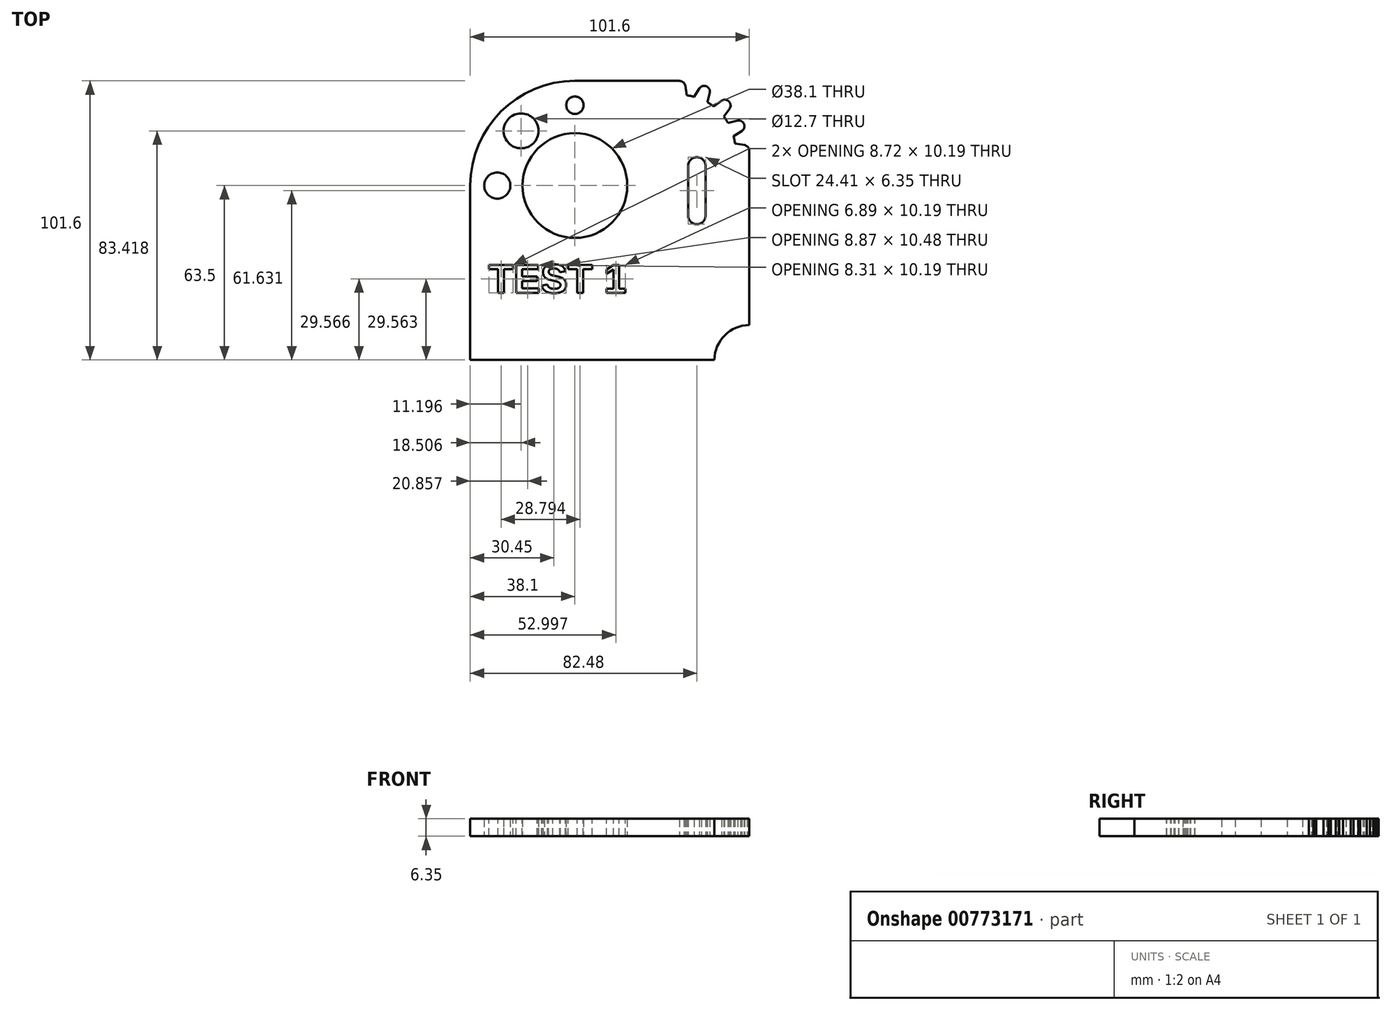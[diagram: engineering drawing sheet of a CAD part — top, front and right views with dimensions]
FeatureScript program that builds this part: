
annotation { "Feature Type Name" : "Feature", "Feature Type Description" : "" }
export const myFeature = defineFeature(function(context is Context, id is Id, definition is map)
    precondition{}
    {
        {
            var Q0;
            Q0=qCreatedBy(makeId("Top.planeOp"),FACE);
            var sketch = newSketch(context, id + "F0", { "sketchPlane" : qUnion([Q0])});
            skLineSegment(sketch, "E0.bottom", {"start": v(-12.7, 0) * mm, "end": v(-101.6, 0) * mm});
            skLineSegment(sketch, "E0.top", {"start": v(-25.4, 101.6) * mm, "end": v(-63.5, 101.6) * mm});
            skLineSegment(sketch, "E0.left", {"start": v(0, 12.7) * mm, "end": v(0, 76.2) * mm});
            skLineSegment(sketch, "E0.right", {"start": v(-101.6, 0) * mm, "end": v(-101.6, 63.5) * mm});
            skPoint(sketch, "E1.visualSharp", {"position": v(-101.6, 101.6) * mm});
            skArc(sketch, "E1.filletArc", {"start": v(-63.5, 101.6) * mm, "mid": v(-90.44, 90.44) * mm, "end": v(-101.6, 63.5) * mm});
            skArc(sketch, "E2.0", {"start": v(-5.08, 76.2) * mm, "mid": v(-11.03, 90.57) * mm, "end": v(-25.4, 96.52) * mm});
            skLineSegment(sketch, "E3", {"start": v(-25.4, 96.52) * mm, "end": v(-25.4, 101.6) * mm});
            skLineSegment(sketch, "E4", {"start": v(-5.08, 76.2) * mm, "end": v(0, 76.2) * mm});
            skLineSegment(sketch, "E5", {"start": v(-22.77, 96.35) * mm, "end": v(-23.3, 99.9) * mm});
            skLineSegment(sketch, "E6", {"start": v(-23.3, 99.9) * mm, "end": v(-23.77, 100.84) * mm});
            skArc(sketch, "E7", {"start": v(-23.77, 100.84) * mm, "mid": v(-24.52, 101.35) * mm, "end": v(-25.4, 101.6) * mm});
            skLineSegment(sketch, "E8.1.0", {"start": v(-15.26, 93.81) * mm, "end": v(-14.4, 97.29) * mm});
            skLineSegment(sketch, "E8.1.1", {"start": v(-14.4, 97.29) * mm, "end": v(-14.47, 98.34) * mm});
            skArc(sketch, "E8.1.2", {"start": v(-14.47, 98.34) * mm, "mid": v(-14.96, 99.1) * mm, "end": v(-15.68, 99.67) * mm});
            skArc(sketch, "E8.1.3", {"start": v(-17.48, 99.58) * mm, "mid": v(-16.59, 99.78) * mm, "end": v(-15.68, 99.67) * mm});
            skLineSegment(sketch, "E8.1.4", {"start": v(-18.27, 98.9) * mm, "end": v(-17.48, 99.58) * mm});
            skLineSegment(sketch, "E8.1.5", {"start": v(-20.12, 95.82) * mm, "end": v(-18.27, 98.9) * mm});
            skLineSegment(sketch, "E8.2.0", {"start": v(-9.3, 88.59) * mm, "end": v(-7.16, 91.47) * mm});
            skLineSegment(sketch, "E8.2.1", {"start": v(-7.16, 91.47) * mm, "end": v(-6.83, 92.47) * mm});
            skArc(sketch, "E8.2.2", {"start": v(-6.83, 92.47) * mm, "mid": v(-7, 93.36) * mm, "end": v(-7.44, 94.16) * mm});
            skArc(sketch, "E8.2.3", {"start": v(-9.13, 94.77) * mm, "mid": v(-8.24, 94.6) * mm, "end": v(-7.44, 94.16) * mm});
            skLineSegment(sketch, "E8.2.4", {"start": v(-10.13, 94.44) * mm, "end": v(-9.13, 94.77) * mm});
            skLineSegment(sketch, "E8.2.5", {"start": v(-13.01, 92.3) * mm, "end": v(-10.13, 94.44) * mm});
            skLineSegment(sketch, "E8.3.0", {"start": v(-5.78, 81.48) * mm, "end": v(-2.7, 83.33) * mm});
            skLineSegment(sketch, "E8.3.1", {"start": v(-2.7, 83.33) * mm, "end": v(-2.02, 84.12) * mm});
            skArc(sketch, "E8.3.2", {"start": v(-2.02, 84.12) * mm, "mid": v(-1.82, 85.01) * mm, "end": v(-1.93, 85.92) * mm});
            skArc(sketch, "E8.3.3", {"start": v(-3.26, 87.13) * mm, "mid": v(-2.5, 86.64) * mm, "end": v(-1.93, 85.92) * mm});
            skLineSegment(sketch, "E8.3.4", {"start": v(-4.31, 87.2) * mm, "end": v(-3.26, 87.13) * mm});
            skLineSegment(sketch, "E8.3.5", {"start": v(-7.79, 86.34) * mm, "end": v(-4.31, 87.2) * mm});
            skArc(sketch, "E8.4.3", {"start": v(-0.76, 77.83) * mm, "mid": v(-0.25, 77.08) * mm, "end": v(0, 76.2) * mm});
            skLineSegment(sketch, "E8.4.4", {"start": v(-1.7, 78.3) * mm, "end": v(-0.76, 77.83) * mm});
            skLineSegment(sketch, "E8.4.5", {"start": v(-5.25, 78.83) * mm, "end": v(-1.7, 78.3) * mm});
            skLineSegment(sketch, "E8.anchor1", {"start": v(-25.4, 76.2) * mm, "end": v(-25.4, 101.6) * mm, "construction": true});
            skLineSegment(sketch, "E8.anchor2", {"start": v(-25.4, 76.2) * mm, "end": v(0, 76.2) * mm, "construction": true});
            skArc(sketch, "E9", {"start": v(0, 12.7) * mm, "mid": v(-8.98, 8.98) * mm, "end": v(-12.7, 0) * mm});
            skCircle(sketch, "E10", {"center": v(-63.5, 63.5) * mm, "radius": 19.05 * mm});
            skCircle(sketch, "E11", {"center": v(-63.5, 92.75) * mm, "radius": 3.18 * mm});
            skCircle(sketch, "E12", {"center": v(-91.76, 63.5) * mm, "radius": 4.76 * mm});
            skCircle(sketch, "E13", {"center": v(-83.1, 83.42) * mm, "radius": 6.35 * mm});
            skArc(sketch, "E14", {"start": v(-15.95, 70.66) * mm, "mid": v(-19.12, 73.84) * mm, "end": v(-22.3, 70.66) * mm});
            skArc(sketch, "E15", {"start": v(-22.3, 52.6) * mm, "mid": v(-19.12, 49.42) * mm, "end": v(-15.95, 52.6) * mm});
            skLineSegment(sketch, "E16", {"start": v(-15.95, 52.6) * mm, "end": v(-15.95, 70.66) * mm});
            skLineSegment(sketch, "E17", {"start": v(-22.3, 52.6) * mm, "end": v(-22.3, 70.66) * mm});
            skSolve(sketch);
        }
        {
            var Q0;
            Q0=makeQuery(id+"F0.imprint","IMPRINT",FACE,{"disambiguationData":[TD([[makeQuery(id+"F0.imprint","IMPRINT",EDGE,{"derivedFrom":sQuery(id+"F0.wireOp",EDGE,"E0.bottom")}),-1.0]])]});
            var Q1;
            {var subQ1=sQuery(id+"F0.wireOp",EDGE,"E3");Q1=makeQuery(id+"F0.imprint","IMPRINT",FACE,{"disambiguationData":[TD([[makeQuery(id+"F0.imprint","IMPRINT",EDGE,{"derivedFrom":subQ1}),-1.0]])]});}
            var Q2;
            {var subQ0=sQuery(id+"F0.wireOp",EDGE,"E8.1.0");Q2=makeQuery(id+"F0.imprint","IMPRINT",FACE,{"disambiguationData":[TD([[makeQuery(id+"F0.imprint","IMPRINT",EDGE,{"derivedFrom":subQ0}),1.0]])]});}
            var Q3;
            {var subQ0=sQuery(id+"F0.wireOp",EDGE,"E8.2.0");Q3=makeQuery(id+"F0.imprint","IMPRINT",FACE,{"disambiguationData":[TD([[makeQuery(id+"F0.imprint","IMPRINT",EDGE,{"derivedFrom":subQ0}),1.0]])]});}
            var Q4;
            {var subQ0=sQuery(id+"F0.wireOp",EDGE,"E8.3.0");Q4=makeQuery(id+"F0.imprint","IMPRINT",FACE,{"disambiguationData":[TD([[makeQuery(id+"F0.imprint","IMPRINT",EDGE,{"derivedFrom":subQ0}),1.0]])]});}
            var Q5;
            {var subQ0=sQuery(id+"F0.wireOp",EDGE,"E4");Q5=makeQuery(id+"F0.imprint","IMPRINT",FACE,{"disambiguationData":[TD([[makeQuery(id+"F0.imprint","IMPRINT",EDGE,{"derivedFrom":subQ0}),1.0]])]});}
            extrude(context, id + "F1", {"entities" : qUnion([Q0, Q1, Q2, Q3, Q4, Q5]), "depth" : 6.35 * mm, "offsetDistance" : 25.4 * mm});
        }
        {
            var Q0;
            Q0=makeQuery(id+"F1.opExtrude","CAP_FACE",FACE,{"disambiguationData":[OSD([sQuery(id+"F0.wireOp",EDGE,"E0.bottom"),sQuery(id+"F0.wireOp",EDGE,"E0.top"),sQuery(id+"F0.wireOp",EDGE,"E0.left"),sQuery(id+"F0.wireOp",EDGE,"E0.right"),sQuery(id+"F0.wireOp",EDGE,"E1.filletArc"),sQuery(id+"F0.wireOp",EDGE,"E2.0"),sQuery(id+"F0.wireOp",EDGE,"E5"),sQuery(id+"F0.wireOp",EDGE,"E6"),sQuery(id+"F0.wireOp",EDGE,"E7"),sQuery(id+"F0.wireOp",EDGE,"E8.1.0"),sQuery(id+"F0.wireOp",EDGE,"E8.1.1"),sQuery(id+"F0.wireOp",EDGE,"E8.1.2"),sQuery(id+"F0.wireOp",EDGE,"E8.1.3"),sQuery(id+"F0.wireOp",EDGE,"E8.1.4"),sQuery(id+"F0.wireOp",EDGE,"E8.1.5"),sQuery(id+"F0.wireOp",EDGE,"E8.2.0"),sQuery(id+"F0.wireOp",EDGE,"E8.2.1"),sQuery(id+"F0.wireOp",EDGE,"E8.2.2"),sQuery(id+"F0.wireOp",EDGE,"E8.2.3"),sQuery(id+"F0.wireOp",EDGE,"E8.2.4"),sQuery(id+"F0.wireOp",EDGE,"E8.2.5"),sQuery(id+"F0.wireOp",EDGE,"E8.3.0"),sQuery(id+"F0.wireOp",EDGE,"E8.3.1"),sQuery(id+"F0.wireOp",EDGE,"E8.3.2"),sQuery(id+"F0.wireOp",EDGE,"E8.3.3"),sQuery(id+"F0.wireOp",EDGE,"E8.3.4"),sQuery(id+"F0.wireOp",EDGE,"E8.3.5"),sQuery(id+"F0.wireOp",EDGE,"E8.4.3"),sQuery(id+"F0.wireOp",EDGE,"E8.4.4"),sQuery(id+"F0.wireOp",EDGE,"E8.4.5"),sQuery(id+"F0.wireOp",EDGE,"E9"),sQuery(id+"F0.wireOp",EDGE,"E10"),sQuery(id+"F0.wireOp",EDGE,"E11"),sQuery(id+"F0.wireOp",EDGE,"E12"),sQuery(id+"F0.wireOp",EDGE,"E13"),sQuery(id+"F0.wireOp",EDGE,"E14"),sQuery(id+"F0.wireOp",EDGE,"E15"),sQuery(id+"F0.wireOp",EDGE,"E16"),sQuery(id+"F0.wireOp",EDGE,"E17")])],"isStart":false});
            var sketch = newSketch(context, id + "F2", { "sketchPlane" : qUnion([Q0])});
            skText(sketch, "E18", { "text": "TEST 1", "fontName": "Arimo-Bold.ttf"});
            const initialGuessF2  = {"E18": [-0.09493, 0.02447, 1, 0, 0.01066]};
            skSetInitialGuess(sketch, initialGuessF2);
            skSolve(sketch);
        }
        {
            var Q0;
            Q0 = qSketchRegion(id + "F2", true);
            extrude(context, id + "F3", {"entities" : qUnion([Q0]), "operationType" : NewBodyOperationType.REMOVE, "oppositeDirection" : true, "depth" : 25.4 * mm, "offsetDistance" : 25.4 * mm});
        }
    });
